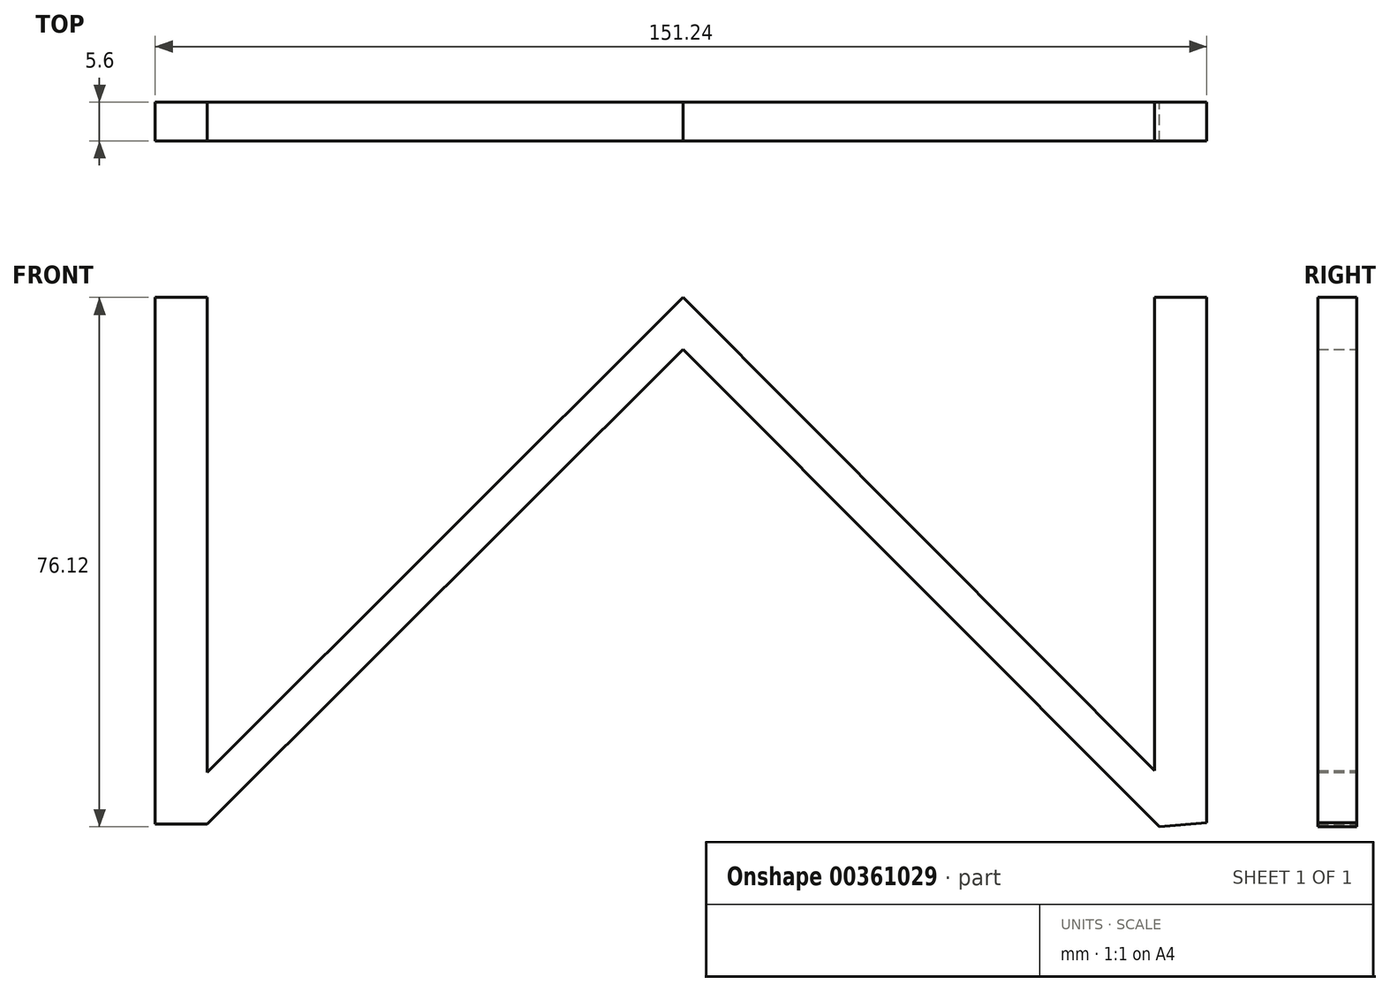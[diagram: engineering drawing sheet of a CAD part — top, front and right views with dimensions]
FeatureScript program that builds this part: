
annotation { "Feature Type Name" : "Feature", "Feature Type Description" : "" }
export const myFeature = defineFeature(function(context is Context, id is Id, definition is map)
    precondition{}
    {
        {
            var Q0;
            Q0=qCreatedBy(makeId("Front.planeOp"),FACE);
            var sketch = newSketch(context, id + "F0", { "sketchPlane" : qUnion([Q0])});
            skLineSegment(sketch, "E0", {"start": v(0, 0) * mm, "end": v(75.3, 0) * mm});
            skLineSegment(sketch, "E1", {"start": v(75.3, 0) * mm, "end": v(75.3, -75.51) * mm});
            skLineSegment(sketch, "E2", {"start": v(75.3, -75.51) * mm, "end": v(0, 0) * mm});
            skLineSegment(sketch, "E3", {"start": v(0, 0) * mm, "end": v(-75.93, -75.72) * mm});
            skLineSegment(sketch, "E4", {"start": v(-75.93, -75.72) * mm, "end": v(-75.93, 0) * mm});
            skLineSegment(sketch, "E5", {"start": v(-75.93, 0) * mm, "end": v(0, 0) * mm});
            skLineSegment(sketch, "E6", {"start": v(67.84, 0) * mm, "end": v(67.84, -68.03) * mm});
            skLineSegment(sketch, "E7", {"start": v(67.84, -68.03) * mm, "end": v(0, 0) * mm});
            skLineSegment(sketch, "E8", {"start": v(-68.46, 0) * mm, "end": v(-68.46, -68.27) * mm});
            skLineSegment(sketch, "E9", {"start": v(-68.46, -75.72) * mm, "end": v(0, -7.45) * mm});
            skLineSegment(sketch, "E10", {"start": v(0, -7.45) * mm, "end": v(0, 0) * mm});
            skLineSegment(sketch, "E11", {"start": v(0, -7.45) * mm, "end": v(68.48, -76.12) * mm});
            skLineSegment(sketch, "E12", {"start": v(68.48, -76.12) * mm, "end": v(75.3, -75.51) * mm});
            skLineSegment(sketch, "E13", {"start": v(-68.46, -75.72) * mm, "end": v(-75.93, -75.72) * mm});
            skLineSegment(sketch, "E14", {"start": v(-75.93, 0) * mm, "end": v(-75.93, 10.13) * mm});
            skLineSegment(sketch, "E15", {"start": v(-75.93, 10.13) * mm, "end": v(75.34, 10.13) * mm});
            skLineSegment(sketch, "E16", {"start": v(75.34, 10.13) * mm, "end": v(75.3, 0) * mm});
            skSolve(sketch);
        }
        {
            var Q0;
            Q0=makeQuery(id+"F0.imprint","IMPRINT",FACE,{"disambiguationData":[TD([[makeQuery(id+"F0.imprint","IMPRINT",EDGE,{"derivedFrom":sQuery(id+"F0.wireOp",EDGE,"E9")}),1.0]])]});
            var Q1;
            {var subQ0=sQuery(id+"F0.wireOp",EDGE,"E1");Q1=makeQuery(id+"F0.imprint","IMPRINT",FACE,{"disambiguationData":[TD([[makeQuery(id+"F0.imprint","IMPRINT",EDGE,{"derivedFrom":subQ0}),-1.0]])]});}
            var Q2;
            {var subQ0=sQuery(id+"F0.wireOp",EDGE,"E4");Q2=makeQuery(id+"F0.imprint","IMPRINT",FACE,{"disambiguationData":[TD([[makeQuery(id+"F0.imprint","IMPRINT",EDGE,{"derivedFrom":subQ0}),-1.0]])]});}
            var Q3;
            Q3=makeQuery(id+"F0.imprint","IMPRINT",FACE,{"disambiguationData":[TD([[makeQuery(id+"F0.imprint","IMPRINT",EDGE,{"derivedFrom":sQuery(id+"F0.wireOp",EDGE,"E2")}),1.0]])]});
            var Q4;
            Q4=makeQuery(id+"F0.imprint","IMPRINT",FACE,{"disambiguationData":[TD([[makeQuery(id+"F0.imprint","IMPRINT",EDGE,{"derivedFrom":sQuery(id+"F0.wireOp",EDGE,"E2")}),1.0]])]});
            var Q5;
            Q5=makeQuery(id+"F0.imprint","IMPRINT",FACE,{"disambiguationData":[TD([[makeQuery(id+"F0.imprint","IMPRINT",EDGE,{"derivedFrom":sQuery(id+"F0.wireOp",EDGE,"E9")}),1.0]])]});
            var Q6;
            {var subQ0=sQuery(id+"F0.wireOp",EDGE,"E1");Q6=makeQuery(id+"F0.imprint","IMPRINT",FACE,{"disambiguationData":[TD([[makeQuery(id+"F0.imprint","IMPRINT",EDGE,{"derivedFrom":subQ0}),-1.0]])]});}
            var Q7;
            {var subQ0=sQuery(id+"F0.wireOp",EDGE,"E4");Q7=makeQuery(id+"F0.imprint","IMPRINT",FACE,{"disambiguationData":[TD([[makeQuery(id+"F0.imprint","IMPRINT",EDGE,{"derivedFrom":subQ0}),-1.0]])]});}
            extrude(context, id + "F1", {"entities" : qUnion([Q0, Q1, Q2, Q3, Q4, Q5, Q6, Q7]), "depth" : 5.6 * mm});
        }
    });
